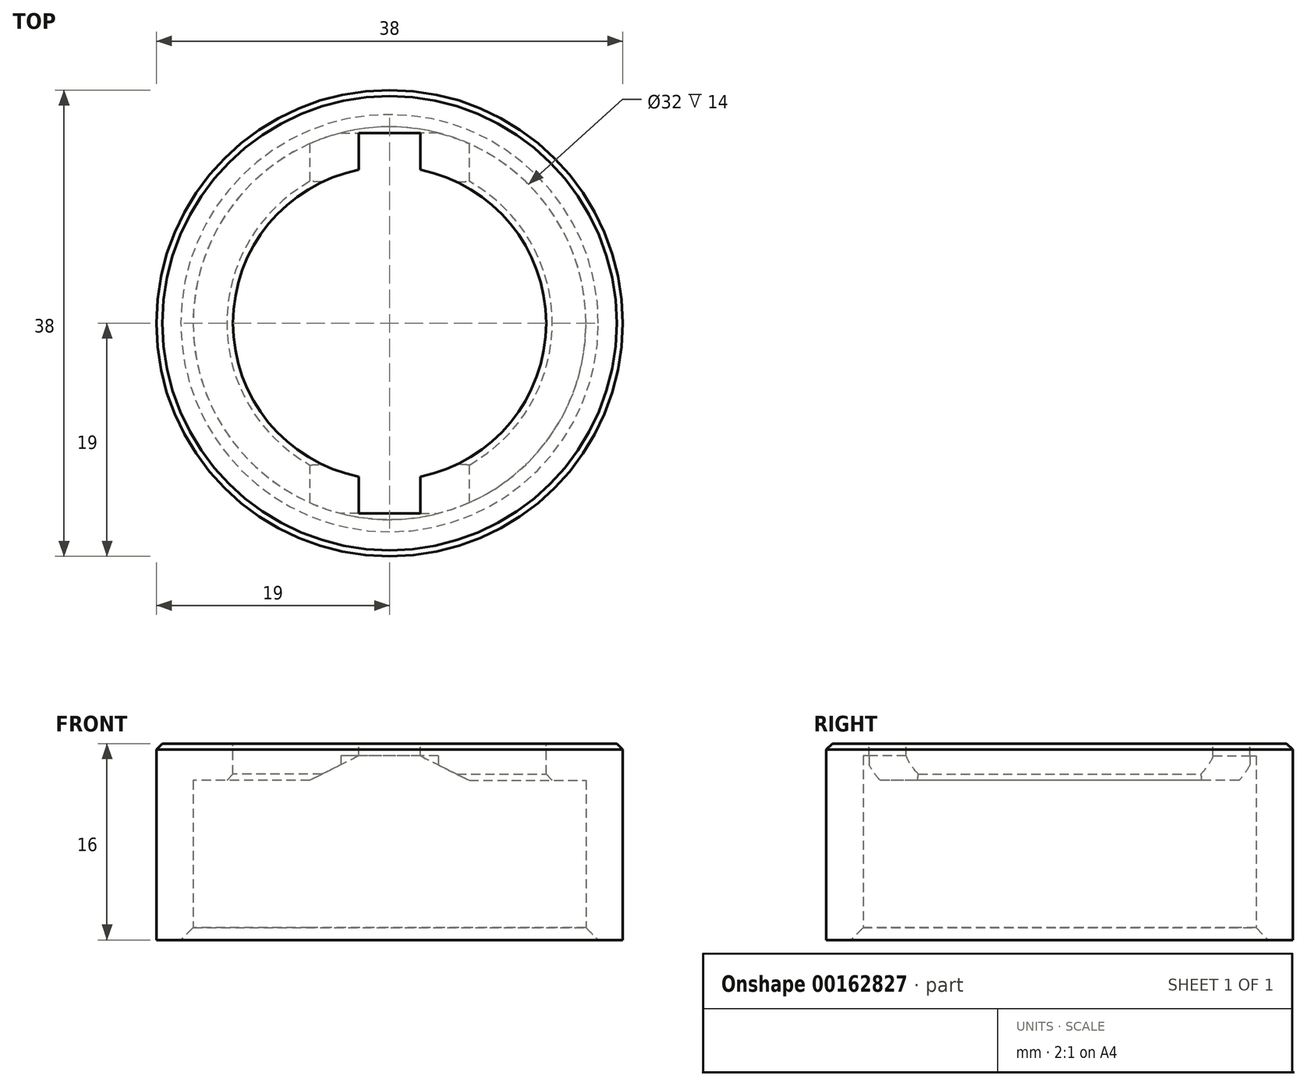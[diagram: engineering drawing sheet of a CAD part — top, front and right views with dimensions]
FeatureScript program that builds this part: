
annotation { "Feature Type Name" : "Feature", "Feature Type Description" : "" }
export const myFeature = defineFeature(function(context is Context, id is Id, definition is map)
    precondition{}
    {
        {
            var Q0;
            Q0=qCreatedBy(makeId("Top.planeOp"),FACE);
            var sketch = newSketch(context, id + "F0", { "sketchPlane" : qUnion([Q0])});
            skCircle(sketch, "E0", {"center": v(0, 0) * mm, "radius": 16 * mm});
            skSolve(sketch);
        }
        {
            var Q0;
            Q0=makeQuery(id+"F0.imprint","IMPRINT",FACE,{"disambiguationData":[TD([[makeQuery(id+"F0.imprint","IMPRINT",EDGE,{"derivedFrom":sQuery(id+"F0.wireOp",EDGE,"E0")}),1.0]])]});
            extrude(context, id + "F1", {"entities" : qUnion([Q0]), "depth" : 13 * mm});
        }
        {
            var Q0;
            Q0=makeQuery(id+"F1.opExtrude","CAP_FACE",FACE,{"disambiguationData":[OSD([sQuery(id+"F0.wireOp",EDGE,"E0")])],"isStart":true});
            shell(context, id + "F2", {"entities" : qUnion([Q0]), "thickness" : 3 * mm, "oppositeDirection" : true});
        }
        {
            var Q0;
            {var subQ0=sQuery(id+"F0.wireOp",EDGE,"E0");Q0=makeQuery(id+"F2.opShell","OFFSET_EDGE",EDGE,{"disambiguationData":[OSD([subQ0]),TDD([makeQuery(id+"F1.opExtrude","CAP_EDGE",EDGE,{"disambiguationData":[OSD([subQ0])],"isStart":true})])]});}
            chamfer(context, id + "F3", {"entities" : qUnion([Q0]), "width" : 1 * mm, "tangentPropagation" : true});
        }
        {
            var Q0;
            Q0=makeQuery(id+"F1.opExtrude","CAP_FACE",FACE,{"disambiguationData":[OSD([sQuery(id+"F0.wireOp",EDGE,"E0")])],"isStart":false});
            var sketch = newSketch(context, id + "F4", { "sketchPlane" : qUnion([Q0])});
            skCircle(sketch, "E1", {"center": v(0, 0) * mm, "radius": 12.75 * mm});
            skSolve(sketch);
        }
        {
            var Q0;
            Q0=makeQuery(id+"F4.imprint","IMPRINT",FACE,{"disambiguationData":[TD([[makeQuery(id+"F4.imprint","IMPRINT",EDGE,{"derivedFrom":sQuery(id+"F4.wireOp",EDGE,"E1")}),1.0]])]});
            extrude(context, id + "F5", {"entities" : qUnion([Q0]), "operationType" : NewBodyOperationType.REMOVE, "oppositeDirection" : true, "depth" : 25 * mm});
        }
        {
            var Q0;
            Q0=makeQuery(id+"F5.boolean.opBoolean","COPY",EDGE,{"derivedFrom":makeQuery(id+"F5.opExtrude","CAP_EDGE",EDGE,{"disambiguationData":[OSD([sQuery(id+"F4.wireOp",EDGE,"E1")])],"isStart":true})});
            var Q1;
            {var subQ0=sQuery(id+"F0.wireOp",EDGE,"E0");Q1=makeQuery(id+"F5.boolean.opBoolean","INTERSECT",EDGE,{"derivedFrom":[makeQuery(id+"F2.opShell","OFFSET_FACE",FACE,{"disambiguationData":[OSD([subQ0]),TDD([makeQuery(id+"F1.opExtrude","CAP_FACE",FACE,{"disambiguationData":[OSD([subQ0])],"isStart":false})])]}),makeQuery(id+"F5.opExtrude","SWEPT_FACE",FACE,{"disambiguationData":[OSD([sQuery(id+"F4.wireOp",EDGE,"E1")])]})]});}
            chamfer(context, id + "F6", {"entities" : qUnion([Q0, Q1]), "width" : 0.5 * mm, "tangentPropagation" : true});
        }
        {
            var Q0;
            Q0=makeQuery(id+"F1.opExtrude","CAP_EDGE",EDGE,{"disambiguationData":[OSD([sQuery(id+"F0.wireOp",EDGE,"E0")])],"isStart":false});
            chamfer(context, id + "F7", {"entities" : qUnion([Q0]), "width" : 0.5 * mm, "tangentPropagation" : true});
        }
        {
            var Q0;
            Q0=makeQuery(id+"F1.opExtrude","CAP_FACE",FACE,{"disambiguationData":[OSD([sQuery(id+"F0.wireOp",EDGE,"E0")])],"isStart":false});
            var sketch = newSketch(context, id + "F8", { "sketchPlane" : qUnion([Q0])});
            skLineSegment(sketch, "E2.bottom", {"start": v(2.5, 15.5) * mm, "end": v(-2.5, 15.5) * mm});
            skLineSegment(sketch, "E2.top", {"start": v(2.5, -15.5) * mm, "end": v(-2.5, -15.5) * mm});
            skLineSegment(sketch, "E2.left", {"start": v(2.5, 15.5) * mm, "end": v(2.5, -15.5) * mm});
            skLineSegment(sketch, "E2.right", {"start": v(-2.5, 15.5) * mm, "end": v(-2.5, -15.5) * mm});
            skPoint(sketch, "E2.middle", {"position": v(0, 0) * mm});
            skSolve(sketch);
        }
        {
            var Q0;
            {var subQ0=sQuery(id+"F8.wireOp",EDGE,"E2.top");Q0=makeQuery(id+"F8.imprint","IMPRINT",FACE,{"disambiguationData":[TD([[makeQuery(id+"F8.imprint","IMPRINT",EDGE,{"derivedFrom":subQ0}),-1.0]])]});}
            var Q1;
            {var subQ0=sQuery(id+"F8.wireOp",EDGE,"E2.bottom");Q1=makeQuery(id+"F8.imprint","IMPRINT",FACE,{"disambiguationData":[TD([[makeQuery(id+"F8.imprint","IMPRINT",EDGE,{"derivedFrom":subQ0}),1.0]])]});}
            var Q2;
            {var subQ0=sQuery(id+"F8.wireOp",EDGE,"E2.left");var subQ1=makeQuery(id+"F6.opChamfer","BLEND_EDGE",EDGE,{"blendedFrom":[makeQuery(id+"F5.boolean.opBoolean","COPY",EDGE,{"derivedFrom":makeQuery(id+"F5.opExtrude","CAP_EDGE",EDGE,{"disambiguationData":[OSD([sQuery(id+"F4.wireOp",EDGE,"E1")])],"isStart":true})}),makeQuery(id+"F1.opExtrude","CAP_FACE",FACE,{"disambiguationData":[OSD([sQuery(id+"F0.wireOp",EDGE,"E0")])],"isStart":false})],"blendedInto":[makeQuery(id+"F1.opExtrude","CAP_FACE",FACE,{"disambiguationData":[OSD([sQuery(id+"F0.wireOp",EDGE,"E0")])],"isStart":false})]});var subQ2=makeQuery(id+"F8.imprint","INTERSECT",VERTEX,{"disambiguationData":[OD(0.0)],"derivedFrom":[subQ1,subQ0]});Q2=makeQuery(id+"F8.imprint","IMPRINT",FACE,{"disambiguationData":[TD([[makeQuery(id+"F8.imprint","IMPRINT",EDGE,{"disambiguationData":[TD([[subQ2,-1.0]])],"derivedFrom":subQ0}),-1.0]])]});}
            extrude(context, id + "F9", {"entities" : qUnion([Q0, Q1, Q2]), "operationType" : NewBodyOperationType.REMOVE, "oppositeDirection" : true, "depth" : 25 * mm});
        }
        {
            var Q0;
            {var subQ0=sQuery(id+"F0.wireOp",EDGE,"E0");Q0=makeQuery(id+"F9.boolean.opBoolean","INTERSECT",EDGE,{"disambiguationData":[OD(0.0)],"derivedFrom":[makeQuery(id+"F2.opShell","OFFSET_FACE",FACE,{"disambiguationData":[OSD([subQ0]),TDD([makeQuery(id+"F1.opExtrude","CAP_FACE",FACE,{"disambiguationData":[OSD([subQ0])],"isStart":false})])]}),makeQuery(id+"F9.opExtrude","SWEPT_FACE",FACE,{"disambiguationData":[OSD([sQuery(id+"F8.wireOp",EDGE,"E2.left")])]})]});}
            var Q1;
            {var subQ0=sQuery(id+"F0.wireOp",EDGE,"E0");Q1=makeQuery(id+"F9.boolean.opBoolean","INTERSECT",EDGE,{"disambiguationData":[OD(0.0)],"derivedFrom":[makeQuery(id+"F2.opShell","OFFSET_FACE",FACE,{"disambiguationData":[OSD([subQ0]),TDD([makeQuery(id+"F1.opExtrude","CAP_FACE",FACE,{"disambiguationData":[OSD([subQ0])],"isStart":false})])]}),makeQuery(id+"F9.opExtrude","SWEPT_FACE",FACE,{"disambiguationData":[OSD([sQuery(id+"F8.wireOp",EDGE,"E2.right")])]})]});}
            var Q2;
            {var subQ0=sQuery(id+"F0.wireOp",EDGE,"E0");Q2=makeQuery(id+"F9.boolean.opBoolean","INTERSECT",EDGE,{"disambiguationData":[OD(1.0)],"derivedFrom":[makeQuery(id+"F2.opShell","OFFSET_FACE",FACE,{"disambiguationData":[OSD([subQ0]),TDD([makeQuery(id+"F1.opExtrude","CAP_FACE",FACE,{"disambiguationData":[OSD([subQ0])],"isStart":false})])]}),makeQuery(id+"F9.opExtrude","SWEPT_FACE",FACE,{"disambiguationData":[OSD([sQuery(id+"F8.wireOp",EDGE,"E2.left")])]})]});}
            var Q3;
            {var subQ0=sQuery(id+"F0.wireOp",EDGE,"E0");Q3=makeQuery(id+"F9.boolean.opBoolean","INTERSECT",EDGE,{"disambiguationData":[OD(1.0)],"derivedFrom":[makeQuery(id+"F2.opShell","OFFSET_FACE",FACE,{"disambiguationData":[OSD([subQ0]),TDD([makeQuery(id+"F1.opExtrude","CAP_FACE",FACE,{"disambiguationData":[OSD([subQ0])],"isStart":false})])]}),makeQuery(id+"F9.opExtrude","SWEPT_FACE",FACE,{"disambiguationData":[OSD([sQuery(id+"F8.wireOp",EDGE,"E2.right")])]})]});}
            chamfer(context, id + "F10", {"entities" : qUnion([Q0, Q1, Q2, Q3]), "chamferType" : ChamferType.TWO_OFFSETS, "width1" : 2 * mm, "oppositeDirection" : false, "width2" : 4 * mm, "tangentPropagation" : true});
        }
        {
            var Q0;
            {var subQ0=sQuery(id+"F0.wireOp",EDGE,"E0");Q0=makeQuery(id+"F10.opChamfer","SPLIT",FACE,{"disambiguationData":[OD(3.0)],"derivedFrom":makeQuery(id+"F2.opShell","OFFSET_FACE",FACE,{"disambiguationData":[OSD([subQ0]),TDD([makeQuery(id+"F1.opExtrude","CAP_FACE",FACE,{"disambiguationData":[OSD([subQ0])],"isStart":false})])]})});}
            var Q1;
            {var subQ0=sQuery(id+"F0.wireOp",EDGE,"E0");Q1=makeQuery(id+"F10.opChamfer","SPLIT",FACE,{"disambiguationData":[OD(2.0)],"derivedFrom":makeQuery(id+"F2.opShell","OFFSET_FACE",FACE,{"disambiguationData":[OSD([subQ0]),TDD([makeQuery(id+"F1.opExtrude","CAP_FACE",FACE,{"disambiguationData":[OSD([subQ0])],"isStart":false})])]})});}
            extrude(context, id + "F11", {"entities" : qUnion([Q0, Q1]), "operationType" : NewBodyOperationType.REMOVE, "oppositeDirection" : true, "depth" : 2 * mm});
        }
    });
